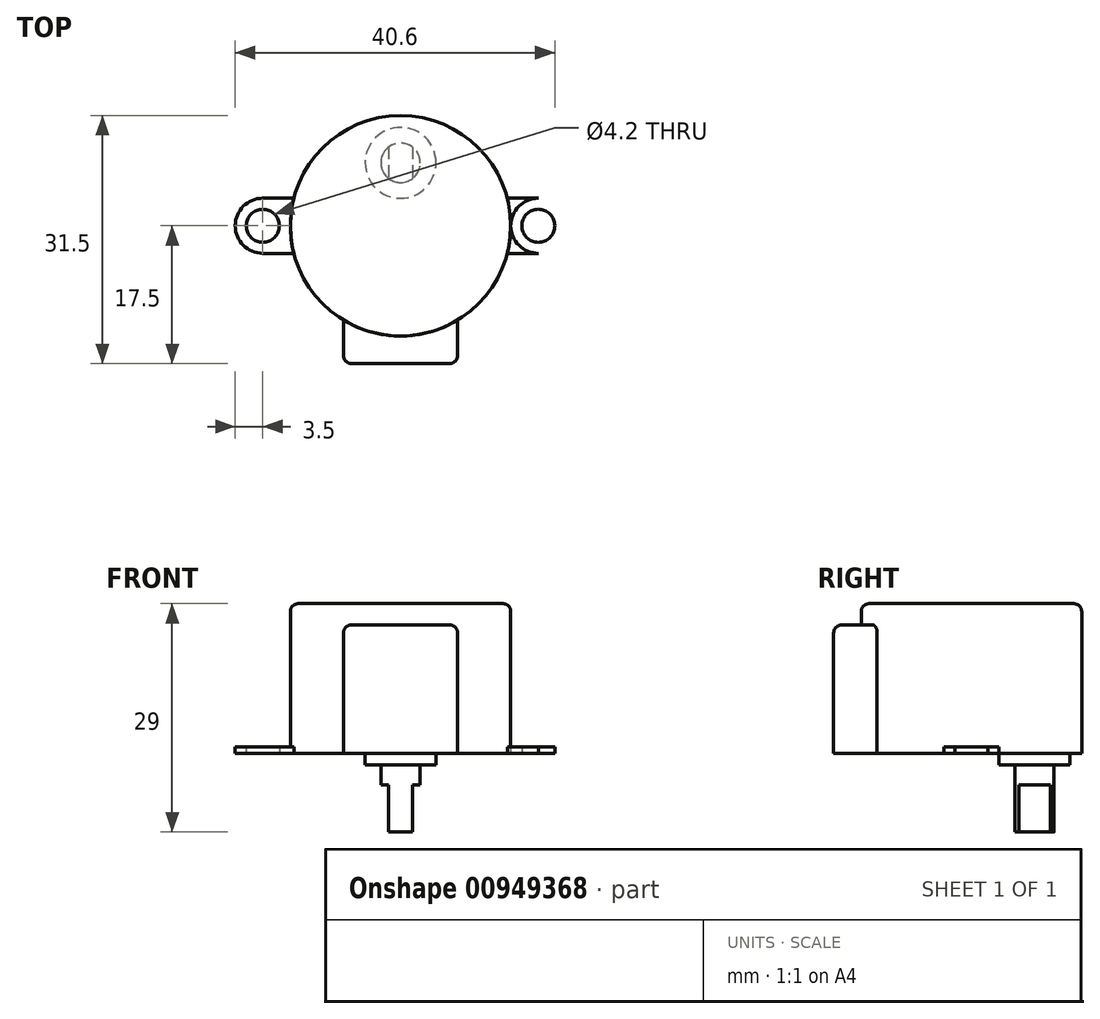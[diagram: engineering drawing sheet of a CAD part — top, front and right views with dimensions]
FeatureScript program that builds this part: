
annotation { "Feature Type Name" : "Feature", "Feature Type Description" : "" }
export const myFeature = defineFeature(function(context is Context, id is Id, definition is map)
    precondition{}
    {
        {
            var Q0;
            Q0=qCreatedBy(makeId("Top.planeOp"),FACE);
            var sketch = newSketch(context, id + "F0", { "sketchPlane" : qUnion([Q0])});
            skCircle(sketch, "E0", {"center": v(0, 0) * mm, "radius": 14 * mm});
            skLineSegment(sketch, "E1", {"start": v(-7.25, -11.98) * mm, "end": v(-7.25, -17.5) * mm});
            skLineSegment(sketch, "E2", {"start": v(-7.25, -17.5) * mm, "end": v(7.25, -17.5) * mm});
            skLineSegment(sketch, "E3", {"start": v(7.25, -17.5) * mm, "end": v(7.25, -11.98) * mm});
            skCircle(sketch, "E4", {"center": v(-17.5, 0) * mm, "radius": 2.1 * mm});
            skCircle(sketch, "E5", {"center": v(-17.5, 0) * mm, "radius": 3.5 * mm});
            skLineSegment(sketch, "E6", {"start": v(-17.5, 3.5) * mm, "end": v(-13.56, 3.5) * mm});
            skLineSegment(sketch, "E7", {"start": v(-17.5, -3.5) * mm, "end": v(-13.56, -3.5) * mm});
            skCircle(sketch, "E8", {"center": v(0, 8) * mm, "radius": 4.5 * mm});
            skLineSegment(sketch, "E9.MirrorCS", {"start": v(17.5, 3.5) * mm, "end": v(13.56, 3.5) * mm});
            skCircle(sketch, "E10.MirrorC", {"center": v(17.5, 0) * mm, "radius": 3.5 * mm});
            skCircle(sketch, "E11.MirrorC", {"center": v(17.5, 0) * mm, "radius": 2.1 * mm});
            skLineSegment(sketch, "E12.MirrorCS", {"start": v(17.5, -3.5) * mm, "end": v(13.56, -3.5) * mm});
            skCircle(sketch, "E13", {"center": v(0, 8) * mm, "radius": 2.5 * mm});
            skCircle(sketch, "E14", {"center": v(0, 8) * mm, "radius": 1.5 * mm, "construction": true});
            skLineSegment(sketch, "E15", {"start": v(1.5, 10) * mm, "end": v(1.5, 6) * mm});
            skLineSegment(sketch, "E16", {"start": v(-1.5, 10) * mm, "end": v(-1.5, 6) * mm});
            skLineSegment(sketch, "E17", {"start": v(0, 8) * mm, "end": v(0, 5.5) * mm, "construction": true});
            skSolve(sketch);
        }
        {
            var Q0;
            Q0=makeQuery(id+"F0.imprint","IMPRINT",FACE,{"disambiguationData":[TD([[makeQuery(id+"F0.imprint","IMPRINT",EDGE,{"derivedFrom":sQuery(id+"F0.wireOp",EDGE,"E8")}),-1.0]])]});
            var Q1;
            Q1=makeQuery(id+"F0.imprint","IMPRINT",FACE,{"disambiguationData":[TD([[makeQuery(id+"F0.imprint","IMPRINT",EDGE,{"derivedFrom":sQuery(id+"F0.wireOp",EDGE,"E8")}),1.0]])]});
            var Q2;
            Q2=makeQuery(id+"F0.imprint","IMPRINT",FACE,{"disambiguationData":[TD([[makeQuery(id+"F0.imprint","IMPRINT",EDGE,{"derivedFrom":sQuery(id+"F0.wireOp",EDGE,"E13")}),1.0]])]});
            var Q3;
            Q3=makeQuery(id+"F0.imprint","IMPRINT",FACE,{"disambiguationData":[TD([[makeQuery(id+"F0.imprint","IMPRINT",EDGE,{"derivedFrom":sQuery(id+"F0.wireOp",EDGE,"E14")}),1.0]])]});
            var Q4;
            {var subQ0=sQuery(id+"F0.wireOp",EDGE,"E15");Q4=makeQuery(id+"F0.imprint","IMPRINT",FACE,{"disambiguationData":[TD([[makeQuery(id+"F0.imprint","IMPRINT",EDGE,{"derivedFrom":subQ0}),1.0]])]});}
            var Q5;
            {var subQ0=sQuery(id+"F0.wireOp",EDGE,"E16");Q5=makeQuery(id+"F0.imprint","IMPRINT",FACE,{"disambiguationData":[TD([[makeQuery(id+"F0.imprint","IMPRINT",EDGE,{"derivedFrom":subQ0}),-1.0]])]});}
            extrude(context, id + "F1", {"entities" : qUnion([Q0, Q1, Q2, Q3, Q4, Q5]), "depth" : 19 * mm, "offsetDistance" : 25 * mm});
        }
        {
            var Q0;
            Q0=makeQuery(id+"F0.imprint","IMPRINT",FACE,{"disambiguationData":[TD([[makeQuery(id+"F0.imprint","IMPRINT",EDGE,{"derivedFrom":sQuery(id+"F0.wireOp",EDGE,"E13")}),1.0]])]});
            extrude(context, id + "F2", {"entities" : qUnion([Q0]), "oppositeDirection" : true, "depth" : 10 * mm, "offsetDistance" : 25 * mm});
        }
        {
            var Q0;
            Q0=makeQuery(id+"F0.imprint","IMPRINT",FACE,{"disambiguationData":[TD([[makeQuery(id+"F0.imprint","IMPRINT",EDGE,{"derivedFrom":sQuery(id+"F0.wireOp",EDGE,"E8")}),1.0]])]});
            extrude(context, id + "F3", {"entities" : qUnion([Q0]), "operationType" : NewBodyOperationType.ADD, "oppositeDirection" : true, "depth" : 1.5 * mm, "offsetDistance" : 25 * mm});
        }
        {
            var Q0;
            {var subQ0=sQuery(id+"F0.wireOp",EDGE,"E12.MirrorCS");Q0=makeQuery(id+"F0.imprint","IMPRINT",FACE,{"disambiguationData":[TD([[makeQuery(id+"F0.imprint","IMPRINT",EDGE,{"derivedFrom":subQ0}),-1.0]])]});}
            var Q1;
            Q1=makeQuery(id+"F0.imprint","IMPRINT",FACE,{"disambiguationData":[TD([[makeQuery(id+"F0.imprint","IMPRINT",EDGE,{"derivedFrom":sQuery(id+"F0.wireOp",EDGE,"E11.MirrorC")}),1.0]])]});
            var Q2;
            {var subQ0=sQuery(id+"F0.wireOp",EDGE,"E9.MirrorCS");Q2=makeQuery(id+"F0.imprint","IMPRINT",FACE,{"disambiguationData":[TD([[makeQuery(id+"F0.imprint","IMPRINT",EDGE,{"derivedFrom":subQ0}),1.0]])]});}
            var Q3;
            {var subQ0=sQuery(id+"F0.wireOp",EDGE,"E7");Q3=makeQuery(id+"F0.imprint","IMPRINT",FACE,{"disambiguationData":[TD([[makeQuery(id+"F0.imprint","IMPRINT",EDGE,{"derivedFrom":subQ0}),1.0]])]});}
            var Q4;
            Q4=makeQuery(id+"F0.imprint","IMPRINT",FACE,{"disambiguationData":[TD([[makeQuery(id+"F0.imprint","IMPRINT",EDGE,{"derivedFrom":sQuery(id+"F0.wireOp",EDGE,"E4")}),-1.0]])]});
            var Q5;
            {var subQ0=sQuery(id+"F0.wireOp",EDGE,"E6");Q5=makeQuery(id+"F0.imprint","IMPRINT",FACE,{"disambiguationData":[TD([[makeQuery(id+"F0.imprint","IMPRINT",EDGE,{"derivedFrom":subQ0}),-1.0]])]});}
            extrude(context, id + "F4", {"entities" : qUnion([Q0, Q1, Q2, Q3, Q4, Q5]), "operationType" : NewBodyOperationType.ADD, "depth" : 0.8 * mm, "offsetDistance" : 25 * mm});
        }
        {
            var Q0;
            {var subQ0=sQuery(id+"F0.wireOp",EDGE,"E1");Q0=makeQuery(id+"F0.imprint","IMPRINT",FACE,{"disambiguationData":[TD([[makeQuery(id+"F0.imprint","IMPRINT",EDGE,{"derivedFrom":subQ0}),1.0]])]});}
            var Q1;
            Q1=makeQuery(id+"F1.opExtrude","CAP_FACE",FACE,{"disambiguationData":[OSD([sQuery(id+"F0.wireOp",EDGE,"E0")])],"isStart":false});
            extrude(context, id + "F5", {"entities" : qUnion([Q0]), "operationType" : NewBodyOperationType.ADD, "endBound" : BoundingType.UP_TO_SURFACE, "depth" : 25 * mm, "endBoundEntityFace" : qUnion([Q1]), "hasOffset" : true, "offsetDistance" : 2.7 * mm});
        }
        {
            var Q0;
            Q0=makeQuery(id+"F1.opExtrude","CAP_EDGE",EDGE,{"disambiguationData":[OSD([sQuery(id+"F0.wireOp",EDGE,"E0")])],"isStart":false});
            var Q1;
            Q1=makeQuery(id+"F5.opExtrude","SWEPT_EDGE",EDGE,{"disambiguationData":[OSD([sQuery(id+"F0.wireOp",EDGE,"E1"),sQuery(id+"F0.wireOp",EDGE,"E2")])]});
            var Q2;
            Q2=makeQuery(id+"F5.opExtrude","SWEPT_EDGE",EDGE,{"disambiguationData":[OSD([sQuery(id+"F0.wireOp",EDGE,"E2"),sQuery(id+"F0.wireOp",EDGE,"E3")])]});
            var Q3;
            Q3=makeQuery(id+"F5.opExtrude","CAP_EDGE",EDGE,{"disambiguationData":[OSD([sQuery(id+"F0.wireOp",EDGE,"E2")])],"isStart":false});
            var Q4;
            Q4=makeQuery(id+"F5.opExtrude","CAP_EDGE",EDGE,{"disambiguationData":[OSD([sQuery(id+"F0.wireOp",EDGE,"E1")])],"isStart":false});
            var Q5;
            Q5=makeQuery(id+"F5.opExtrude","CAP_EDGE",EDGE,{"disambiguationData":[OSD([sQuery(id+"F0.wireOp",EDGE,"E3")])],"isStart":false});
            fillet(context, id + "F6", {"entities" : qUnion([Q0, Q1, Q2, Q3, Q4, Q5]), "radius" : 1 * mm, "tangentPropagation" : true, "allowEdgeOverflow" : false});
        }
        {
            var Q0;
            {var subQ0=sQuery(id+"F0.wireOp",EDGE,"E16");Q0=makeQuery(id+"F0.imprint","IMPRINT",FACE,{"disambiguationData":[TD([[makeQuery(id+"F0.imprint","IMPRINT",EDGE,{"derivedFrom":subQ0}),-1.0]])]});}
            var Q1;
            {var subQ0=sQuery(id+"F0.wireOp",EDGE,"E15");Q1=makeQuery(id+"F0.imprint","IMPRINT",FACE,{"disambiguationData":[TD([[makeQuery(id+"F0.imprint","IMPRINT",EDGE,{"derivedFrom":subQ0}),1.0]])]});}
            extrude(context, id + "F7", {"entities" : qUnion([Q0, Q1]), "operationType" : NewBodyOperationType.ADD, "oppositeDirection" : true, "depth" : 4 * mm, "offsetDistance" : 25 * mm});
        }
        {
            var Q0;
            Q0=makeQuery(id+"F3.boolean.opBoolean","SPLIT",FACE,{"disambiguationData":[TD([makeQuery(id+"F3.opExtrude","SWEPT_FACE",FACE,{"disambiguationData":[OSD([sQuery(id+"F0.wireOp",EDGE,"E13")])]})])],"derivedFrom":makeQuery(id+"F1.opExtrude","CAP_FACE",FACE,{"disambiguationData":[OSD([sQuery(id+"F0.wireOp",EDGE,"E0")])],"isStart":true})});
            var sketch = newSketch(context, id + "F8", { "sketchPlane" : qUnion([Q0])});
            skPoint(sketch, "E18", {"position": v(0, -8) * mm});
            skSolve(sketch);
        }
    });
